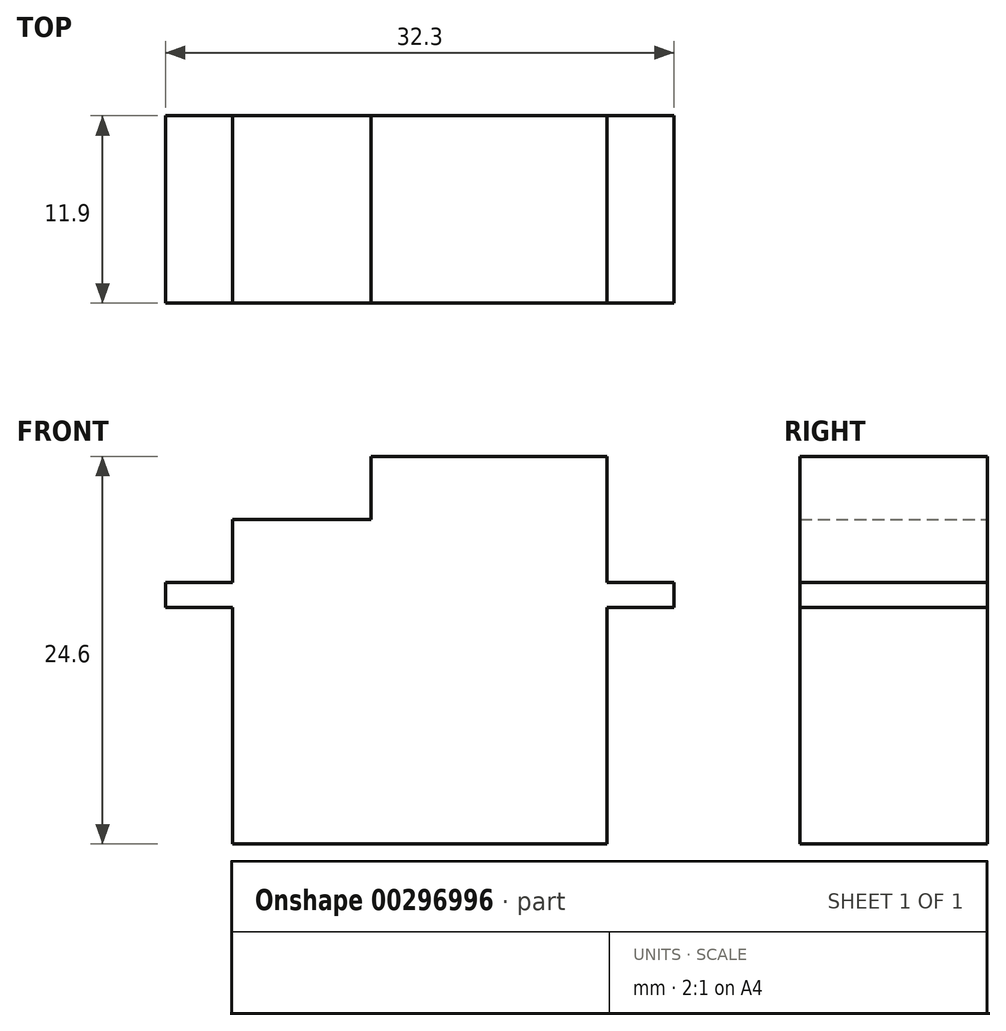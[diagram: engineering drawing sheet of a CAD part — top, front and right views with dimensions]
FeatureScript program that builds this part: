
annotation { "Feature Type Name" : "Feature", "Feature Type Description" : "" }
export const myFeature = defineFeature(function(context is Context, id is Id, definition is map)
    precondition{}
    {
        {
            var Q0;
            Q0=qCreatedBy(makeId("Front.planeOp"),FACE);
            var sketch = newSketch(context, id + "F0", { "sketchPlane" : qUnion([Q0])});
            skLineSegment(sketch, "E0.bottom", {"start": v(0, 5.6) * mm, "end": v(23.8, 5.6) * mm});
            skLineSegment(sketch, "E0.top", {"start": v(0, -15) * mm, "end": v(23.8, -15) * mm});
            skLineSegment(sketch, "E0.left", {"start": v(0, 5.6) * mm, "end": v(0, -15) * mm});
            skLineSegment(sketch, "E0.right", {"start": v(23.8, 5.6) * mm, "end": v(23.8, -15) * mm});
            skLineSegment(sketch, "E1.bottom", {"start": v(-4.25, 1.6) * mm, "end": v(28.05, 1.6) * mm});
            skLineSegment(sketch, "E1.top", {"start": v(-4.25, 0) * mm, "end": v(28.05, 0) * mm});
            skLineSegment(sketch, "E1.left", {"start": v(-4.25, 1.6) * mm, "end": v(-4.25, 0) * mm});
            skLineSegment(sketch, "E1.right", {"start": v(28.05, 1.6) * mm, "end": v(28.05, 0) * mm});
            skLineSegment(sketch, "E2.bottom", {"start": v(8.8, 9.6) * mm, "end": v(23.8, 9.6) * mm});
            skLineSegment(sketch, "E2.top", {"start": v(8.8, 5.6) * mm, "end": v(23.8, 5.6) * mm});
            skLineSegment(sketch, "E2.left", {"start": v(8.8, 9.6) * mm, "end": v(8.8, 5.6) * mm});
            skLineSegment(sketch, "E2.right", {"start": v(23.8, 9.6) * mm, "end": v(23.8, 5.6) * mm});
            skLineSegment(sketch, "E3", {"start": v(11.9, -15) * mm, "end": v(11.9, 0) * mm, "construction": true});
            skPoint(sketch, "E4", {"position": v(0, 0) * mm});
            skSolve(sketch);
        }
        {
            var Q0;
            {var subQ0=sQuery(id+"F0.wireOp",EDGE,"E0.top");Q0=makeQuery(id+"F0.imprint","IMPRINT",FACE,{"disambiguationData":[TD([[makeQuery(id+"F0.imprint","IMPRINT",EDGE,{"derivedFrom":subQ0}),1.0]])]});}
            var Q1;
            {var subQ5=sQuery(id+"F0.wireOp",EDGE,"E0.bottom");Q1=makeQuery(id+"F0.imprint","IMPRINT",FACE,{"disambiguationData":[TD([[makeQuery(id+"F0.imprint","IMPRINT",EDGE,{"derivedFrom":subQ5}),-1.0]])]});}
            var Q2;
            {var subQ5=sQuery(id+"F0.wireOp",EDGE,"E1.left");Q2=makeQuery(id+"F0.imprint","IMPRINT",FACE,{"disambiguationData":[TD([[makeQuery(id+"F0.imprint","IMPRINT",EDGE,{"derivedFrom":subQ5}),1.0]])]});}
            var Q3;
            {var subQ0=sQuery(id+"F0.wireOp",EDGE,"E1.bottom");var subQ1=sQuery(id+"F0.wireOp",EDGE,"E0.left");var subQ2=makeQuery(id+"F0.imprint","INTERSECT",VERTEX,{"derivedFrom":[subQ1,subQ0]});Q3=makeQuery(id+"F0.imprint","IMPRINT",FACE,{"disambiguationData":[TD([[makeQuery(id+"F0.imprint","IMPRINT",EDGE,{"disambiguationData":[TD([[subQ2,-1.0]])],"derivedFrom":subQ1}),1.0]])]});}
            var Q4;
            {var subQ5=sQuery(id+"F0.wireOp",EDGE,"E1.right");Q4=makeQuery(id+"F0.imprint","IMPRINT",FACE,{"disambiguationData":[TD([[makeQuery(id+"F0.imprint","IMPRINT",EDGE,{"derivedFrom":subQ5}),-1.0]])]});}
            var Q5;
            Q5=makeQuery(id+"F0.imprint","IMPRINT",FACE,{"disambiguationData":[TD([[makeQuery(id+"F0.imprint","IMPRINT",EDGE,{"derivedFrom":sQuery(id+"F0.wireOp",EDGE,"E2.bottom")}),-1.0]])]});
            extrude(context, id + "F1", {"entities" : qUnion([Q0, Q1, Q2, Q3, Q4, Q5]), "depth" : 11.9 * mm});
        }
    });
